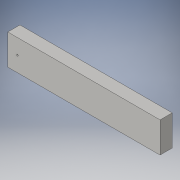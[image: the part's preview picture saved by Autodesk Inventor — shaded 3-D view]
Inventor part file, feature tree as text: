
AUTODESK INVENTOR PART (.ipt)
format: ipt  version: 2016 (Build 200138000, 138)  size: 91,136 bytes
history: native  units: in
note: dims shown in document units (in); Inventor stores cm internally (conversion verified against a paired STEP export)
features: sketch x2, extrude x1, hole x1
ambient origin geometry x8: Origin, YZ Plane, XZ Plane, XY Plane, X Axis, Y Axis, Z Axis, Center Point
bodies: Solid1 (feature_tree)
feature tree (4):
  extrude  "Extrusion1"  Depth=0.7874in
  hole  "Hole1"  [1 undecoded]
  sketch  "Sketch1"  dims[d0=9.8425in d1=0.7874in]
  sketch  "Sketch3"  dims[d2=1.9685in d3=0.0in d4=0.5906in d5=0.0984in d6=0.2953in d7=0.1476in d8=0.0984in d9=90.0deg d10=0.3937in d11=0.8108in]
note: 1 required parameter value undecoded (feature->parameter linkage not recoverable at this tier; creation-order binding heuristic only, values carry confidence <= 0.55)
